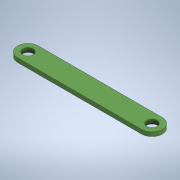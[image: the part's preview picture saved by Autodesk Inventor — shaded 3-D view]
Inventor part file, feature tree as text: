
AUTODESK INVENTOR PART (.ipt)
format: ipt  version: 2020.1 (Build 241239000, 239)  size: 109,568 bytes
history: native  units: in
note: dims shown in document units (in); Inventor stores cm internally (conversion verified against a paired STEP export)
features: extrude x1, sketch x1
ambient origin geometry x8: Origin, YZ Plane, XZ Plane, XY Plane, X Axis, Y Axis, Z Axis, Center Point
bodies: Solid1 (feature_tree)
feature tree (2):
  extrude  "Extrusion1"  Depth=10.0in
  sketch  "Sketch1"  dims[d0=60.0in d1=10.0in d2=5.0in d3=5.0in d4=2.0in d5=0.0in]
